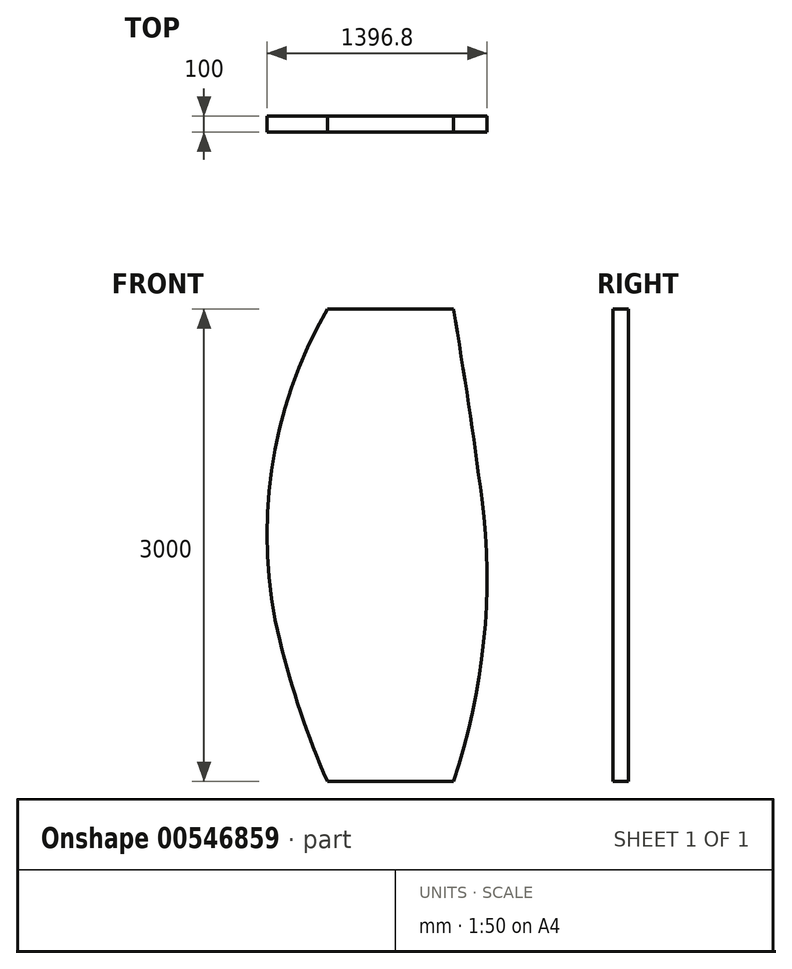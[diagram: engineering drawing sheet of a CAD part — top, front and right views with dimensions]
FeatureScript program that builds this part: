
annotation { "Feature Type Name" : "Feature", "Feature Type Description" : "" }
export const myFeature = defineFeature(function(context is Context, id is Id, definition is map)
    precondition{}
    {
        {
            assignVariable(context, id + "F0", {"name" : "thickness", "anyValue" : 100});
        }
        {
            var Q0;
            Q0=qCreatedBy(makeId("Front.planeOp"),FACE);
            var sketch = newSketch(context, id + "F1", { "sketchPlane" : qUnion([Q0])});
            skLineSegment(sketch, "E0", {"start": v(0, 1615.15) * mm, "end": v(0, -1384.85) * mm, "construction": true});
            skLineSegment(sketch, "E1", {"start": v(-400, -1384.85) * mm, "end": v(400, -1384.85) * mm});
            skLineSegment(sketch, "E2", {"start": v(-400, 1615.15) * mm, "end": v(400, 1615.15) * mm});
            skArc(sketch, "E3", {"start": v(-400, 1615.15) * mm, "mid": v(-754.37, 590.3) * mm, "end": v(-701.6, -492.8) * mm});
            skArc(sketch, "E4", {"start": v(-701.6, -492.8) * mm, "mid": v(-570.11, -945.36) * mm, "end": v(-400, -1384.85) * mm});
            skArc(sketch, "E5", {"start": v(581.4, 408.37) * mm, "mid": v(497.33, 1012.76) * mm, "end": v(400, 1615.15) * mm});
            skArc(sketch, "E6", {"start": v(400, -1384.85) * mm, "mid": v(593.37, -498.62) * mm, "end": v(581.4, 408.37) * mm});
            skLineSegment(sketch, "E7", {"start": v(581.4, 408.37) * mm, "end": v(-701.6, -492.8) * mm, "construction": true});
            skSolve(sketch);
        }
        {
            var Q0;
            Q0 = qSketchRegion(id + "F1", true);
            extrude(context, id + "F2", {"entities" : qUnion([Q0]), "depth" : (getVariable(context, 'thickness')) * mm, "offsetDistance" : 25 * mm});
        }
    });
